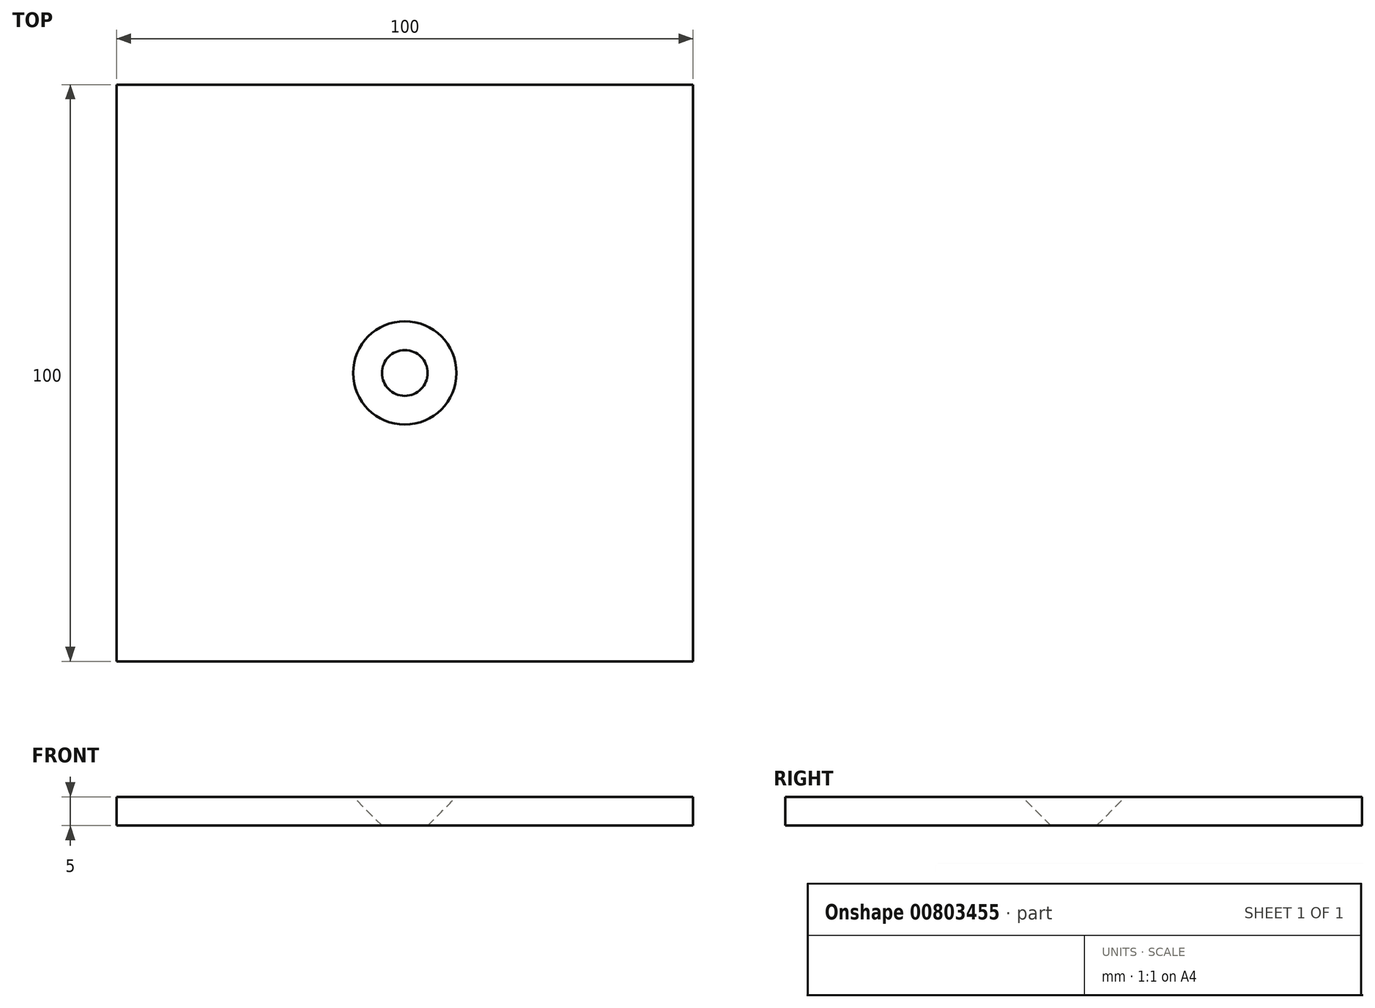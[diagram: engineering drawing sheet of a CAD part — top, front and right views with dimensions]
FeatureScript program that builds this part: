
annotation { "Feature Type Name" : "Feature", "Feature Type Description" : "" }
export const myFeature = defineFeature(function(context is Context, id is Id, definition is map)
    precondition{}
    {
        {
            var Q0;
            Q0=qCreatedBy(makeId("Top.planeOp"),FACE);
            var sketch = newSketch(context, id + "F0", { "sketchPlane" : qUnion([Q0])});
            skLineSegment(sketch, "E0.bottom", {"start": v(50, 50) * mm, "end": v(-50, 50) * mm});
            skLineSegment(sketch, "E0.top", {"start": v(50, -50) * mm, "end": v(-50, -50) * mm});
            skLineSegment(sketch, "E0.left", {"start": v(50, 50) * mm, "end": v(50, -50) * mm});
            skLineSegment(sketch, "E0.right", {"start": v(-50, 50) * mm, "end": v(-50, -50) * mm});
            skPoint(sketch, "E0.middle", {"position": v(0, 0) * mm});
            skSolve(sketch);
        }
        {
            var Q0;
            Q0 = qSketchRegion(id + "F0", true);
            extrude(context, id + "F1", {"entities" : qUnion([Q0]), "depth" : 5 * mm, "offsetDistance" : 25 * mm});
        }
        {
            var Q0;
            Q0=makeQuery(id+"F1.opExtrude","CAP_FACE",FACE,{"disambiguationData":[OSD([sQuery(id+"F0.wireOp",EDGE,"E0.bottom"),sQuery(id+"F0.wireOp",EDGE,"E0.top"),sQuery(id+"F0.wireOp",EDGE,"E0.left"),sQuery(id+"F0.wireOp",EDGE,"E0.right")])],"isStart":false});
            var sketch = newSketch(context, id + "F2", { "sketchPlane" : qUnion([Q0])});
            skPoint(sketch, "E1", {"position": v(0, 0) * mm});
            skSolve(sketch);
        }
        {
            var Q0;
            Q0=sQuery(id+"F2.wireOp",VERTEX,"E1");
            var Q1;
            Q1=makeQuery(id+"F1.opExtrude","SWEPT_BODY",BODY,{"disambiguationData":[OSD([sQuery(id+"F0.wireOp",EDGE,"E0.bottom"),sQuery(id+"F0.wireOp",EDGE,"E0.top"),sQuery(id+"F0.wireOp",EDGE,"E0.left"),sQuery(id+"F0.wireOp",EDGE,"E0.right")])]});
            hole(context, id + "F3", {"style" : HoleStyle.C_SINK, "endStyle" : HoleEndStyle.THROUGH, "standardTappedOrClearance" : lookupTablePath({ "standard" : "ISO", "engagement" : "75%", "pitch" : "1.25 mm", "size" : "M8", "type" : "Tapped" }), "standardBlindInLast" : lookupTablePath({ "standard" : "ISO", "engagement" : "75%", "pitch" : "1.25 mm", "size" : "M8", "type" : "Tapped" }), "holeDiameter" : 6.8 * mm, "cSinkDiameter" : 17.92 * mm, "cSinkAngle" : 90 * degree, "majorDiameter" : 8 * mm, "showTappedDepth" : true, "isTappedThrough" : true, "tappedDepth" : 12 * mm, "tapClearance" : 3, "startFromSketch" : true, "locations" : qUnion([Q0]), "scope" : qUnion([Q1])});
        }
    });
